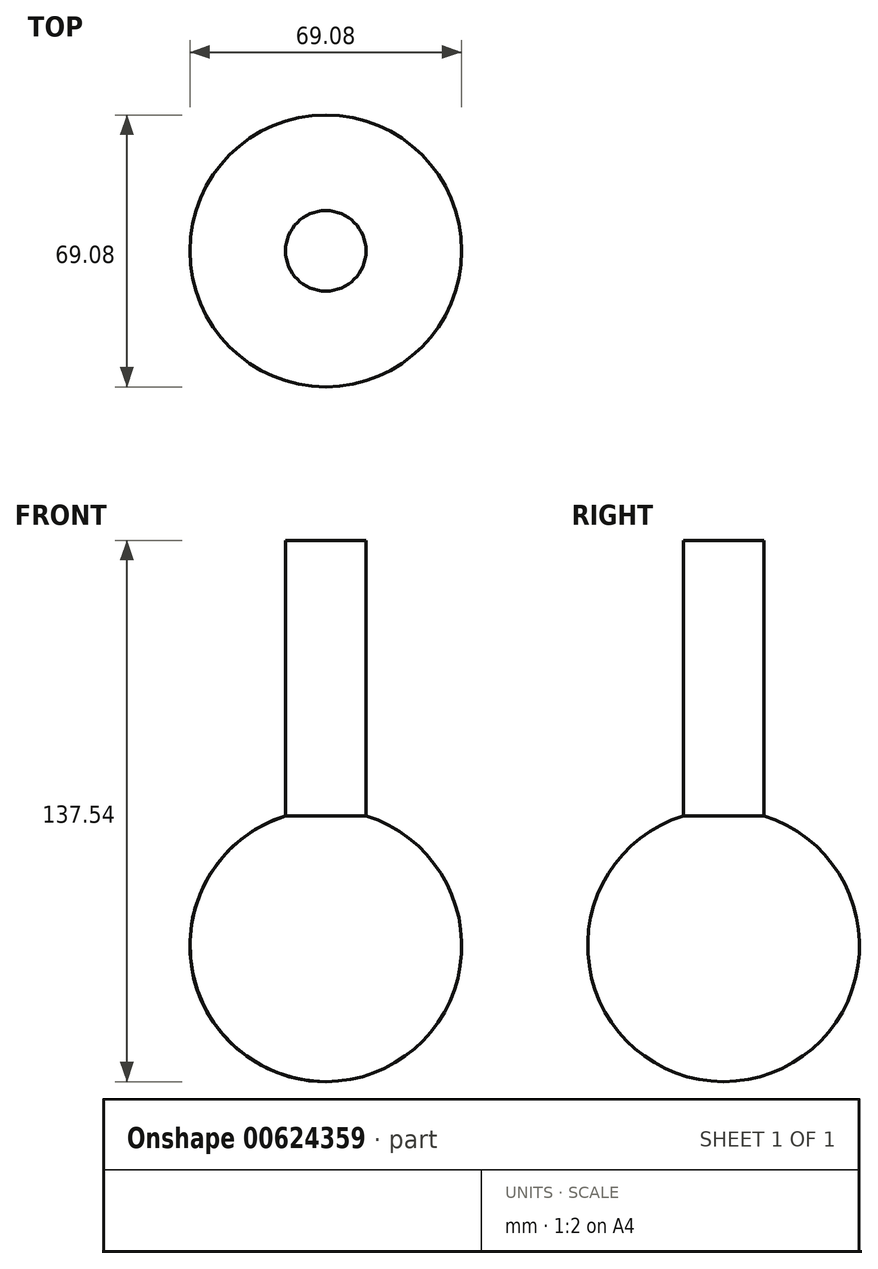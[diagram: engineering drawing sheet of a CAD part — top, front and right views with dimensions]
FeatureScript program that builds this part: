
annotation { "Feature Type Name" : "Feature", "Feature Type Description" : "" }
export const myFeature = defineFeature(function(context is Context, id is Id, definition is map)
    precondition{}
    {
        {
            var Q0;
            Q0=qCreatedBy(makeId("Front.planeOp"),FACE);
            var sketch = newSketch(context, id + "F0", { "sketchPlane" : qUnion([Q0])});
            skArc(sketch, "E0", {"start": v(0, -34.54) * mm, "mid": v(34.54, 0) * mm, "end": v(0, 34.54) * mm});
            skLineSegment(sketch, "E1", {"start": v(0, 34.54) * mm, "end": v(0, -34.54) * mm});
            skSolve(sketch);
        }
        {
            var Q0;
            Q0=makeQuery(id+"F0.imprint","IMPRINT",FACE,{"disambiguationData":[TD([[makeQuery(id+"F0.imprint","IMPRINT",EDGE,{"derivedFrom":sQuery(id+"F0.wireOp",EDGE,"E0")}),1.0]])]});
            var Q1;
            Q1=sQuery(id+"F0.wireOp",EDGE,"E1");
            revolve(context, id + "F1", {"entities" : qUnion([Q0]), "axis" : qUnion([Q1]), "revolveType" : RevolveType.FULL});
        }
        {
            var Q0;
            Q0=qCreatedBy(makeId("Top.planeOp"),FACE);
            var sketch = newSketch(context, id + "F2", { "sketchPlane" : qUnion([Q0])});
            skCircle(sketch, "E2", {"center": v(0, 0) * mm, "radius": 10.23 * mm});
            skSolve(sketch);
        }
        {
            var Q0;
            Q0 = qSketchRegion(id + "F2", true);
            extrude(context, id + "F3", {"entities" : qUnion([Q0]), "operationType" : NewBodyOperationType.ADD, "depth" : 103 * mm, "offsetDistance" : 25 * mm});
        }
    });
